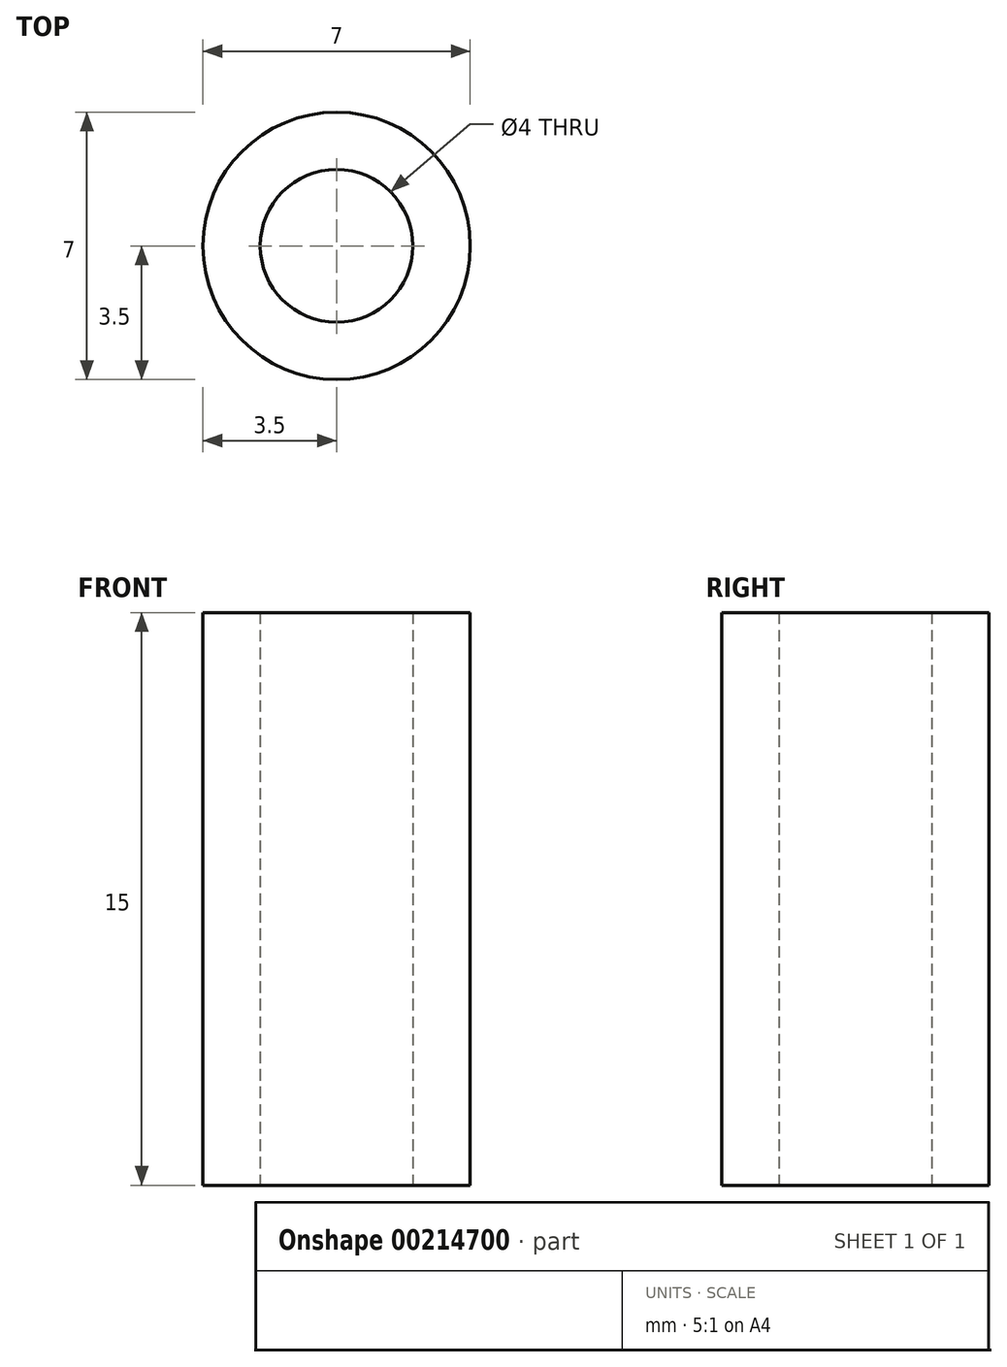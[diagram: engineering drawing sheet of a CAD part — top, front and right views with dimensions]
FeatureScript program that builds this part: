
annotation { "Feature Type Name" : "Feature", "Feature Type Description" : "" }
export const myFeature = defineFeature(function(context is Context, id is Id, definition is map)
    precondition{}
    {
        {
            var Q0;
            Q0=qCreatedBy(makeId("Top.planeOp"),FACE);
            var sketch = newSketch(context, id + "F0", { "sketchPlane" : qUnion([Q0])});
            skCircle(sketch, "E0", {"center": v(0, 0) * mm, "radius": 2 * mm});
            skCircle(sketch, "E1", {"center": v(0, 0) * mm, "radius": 3.5 * mm});
            skSolve(sketch);
        }
        {
            var Q0;
            Q0=makeQuery(id+"F0.imprint","IMPRINT",FACE,{"disambiguationData":[TD([[makeQuery(id+"F0.imprint","IMPRINT",EDGE,{"derivedFrom":sQuery(id+"F0.wireOp",EDGE,"E0")}),-1.0]])]});
            extrude(context, id + "F1", {"entities" : qUnion([Q0]), "depth" : 15 * mm});
        }
    });
